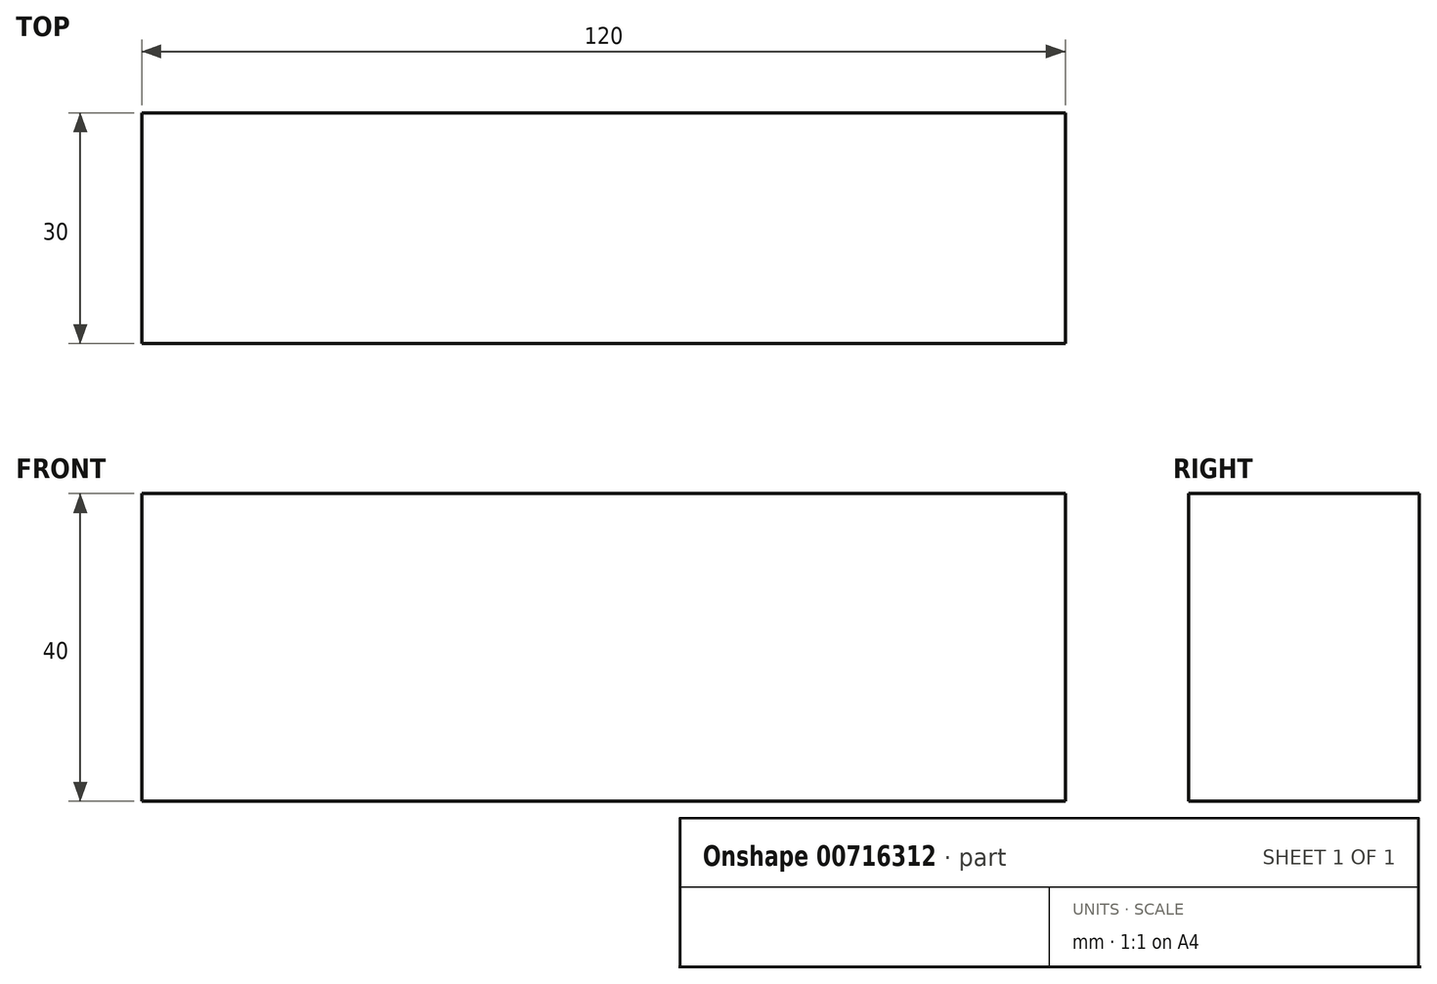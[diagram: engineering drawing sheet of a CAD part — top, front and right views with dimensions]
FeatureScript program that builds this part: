
annotation { "Feature Type Name" : "Feature", "Feature Type Description" : "" }
export const myFeature = defineFeature(function(context is Context, id is Id, definition is map)
    precondition{}
    {
        {
            var Q0;
            Q0=qCreatedBy(makeId("Top.planeOp"),FACE);
            var sketch = newSketch(context, id + "F0", { "sketchPlane" : qUnion([Q0])});
            skLineSegment(sketch, "E0.bottom", {"start": v(60, -15) * mm, "end": v(-60, -15) * mm});
            skLineSegment(sketch, "E0.top", {"start": v(60, 15) * mm, "end": v(-60, 15) * mm});
            skLineSegment(sketch, "E0.left", {"start": v(60, -15) * mm, "end": v(60, 15) * mm});
            skLineSegment(sketch, "E0.right", {"start": v(-60, -15) * mm, "end": v(-60, 15) * mm});
            skPoint(sketch, "E0.middle", {"position": v(0, 0) * mm});
            skSolve(sketch);
        }
        {
            var Q0;
            Q0 = qSketchRegion(id + "F0", true);
            extrude(context, id + "F1", {"entities" : qUnion([Q0]), "depth" : 40 * mm, "offsetDistance" : 25 * mm});
        }
    });
